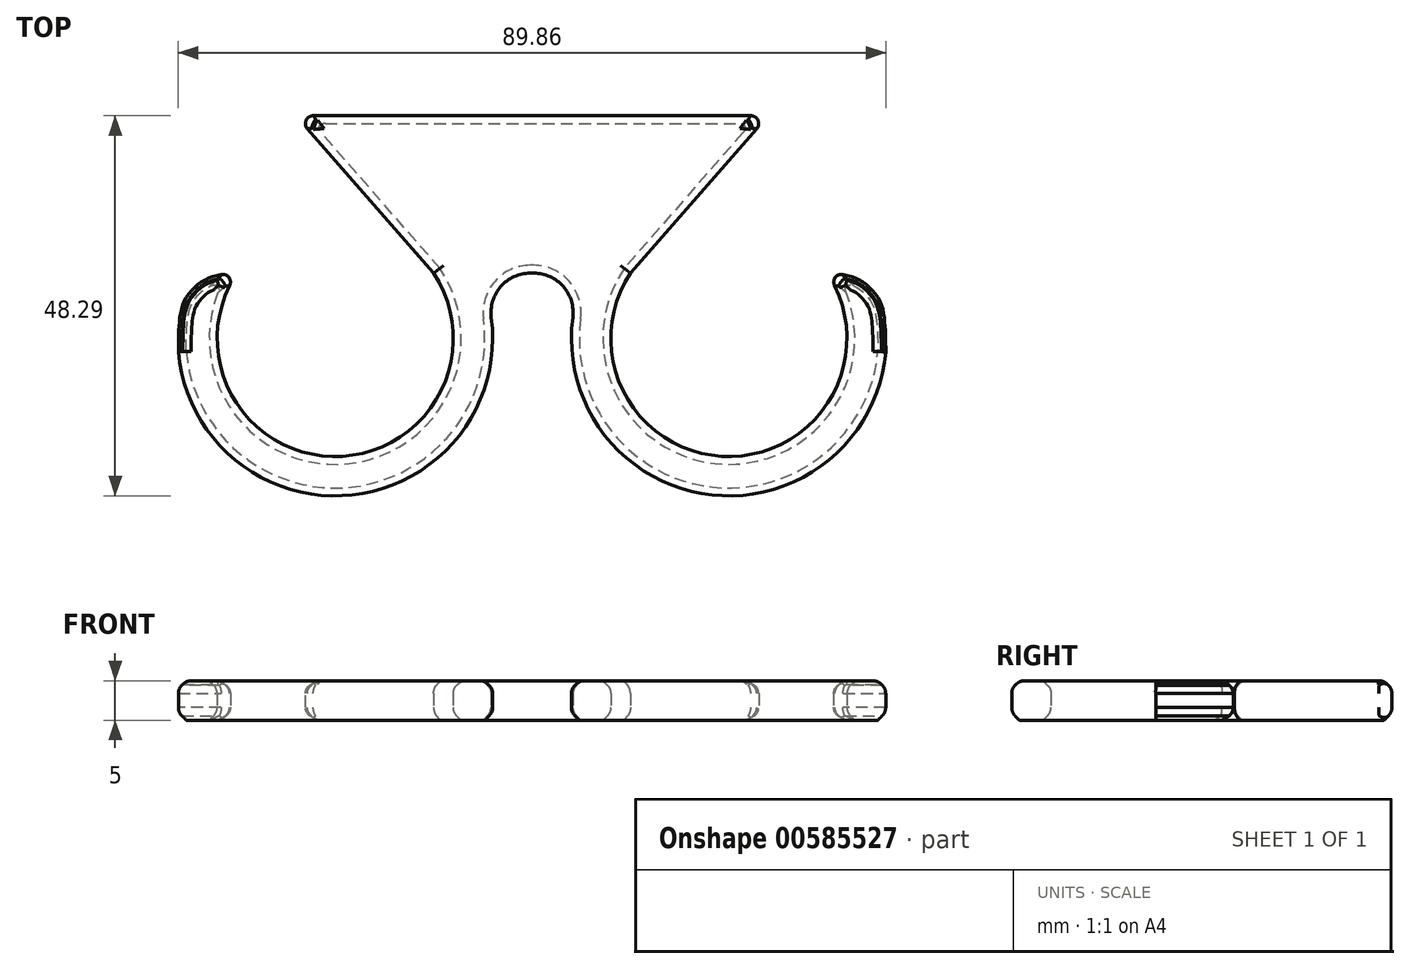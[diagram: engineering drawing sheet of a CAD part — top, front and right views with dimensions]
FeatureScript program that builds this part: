
annotation { "Feature Type Name" : "Feature", "Feature Type Description" : "" }
export const myFeature = defineFeature(function(context is Context, id is Id, definition is map)
    precondition{}
    {
        {
            var Q0;
            Q0=qCreatedBy(makeId("Top.planeOp"),FACE);
            var sketch = newSketch(context, id + "F0", { "sketchPlane" : qUnion([Q0])});
            skLineSegment(sketch, "E0", {"start": v(-30, 20) * mm, "end": v(0, 20) * mm});
            skLineSegment(sketch, "E1", {"start": v(-30, 20) * mm, "end": v(-12.5, 0) * mm});
            skLineSegment(sketch, "E2", {"start": v(-0.22, 0) * mm, "end": v(0, 0) * mm});
            skLineSegment(sketch, "E3", {"start": v(0, 0) * mm, "end": v(0, 20) * mm});
            skArc(sketch, "E4", {"start": v(-37.5, 0) * mm, "mid": v(-25, -23.3) * mm, "end": v(-12.5, 0) * mm});
            skArc(sketch, "E5.0", {"start": v(-44.93, -10) * mm, "mid": v(-22.83, -28.17) * mm, "end": v(-5.17, -5.66) * mm});
            skLineSegment(sketch, "E6", {"start": v(-44.93, -10) * mm, "end": v(-37.5, 0) * mm});
            skLineSegment(sketch, "E7.MirrorCS", {"start": v(30, 20) * mm, "end": v(0, 20) * mm});
            skLineSegment(sketch, "E8.MirrorCS", {"start": v(30, 20) * mm, "end": v(12.5, 0) * mm});
            skLineSegment(sketch, "E9.MirrorCS", {"start": v(0.22, 0) * mm, "end": v(0, 0) * mm});
            skArc(sketch, "E10.MirrorCS", {"start": v(44.93, -10) * mm, "mid": v(22.83, -28.17) * mm, "end": v(5.17, -5.66) * mm});
            skArc(sketch, "E11.MirrorCS", {"start": v(37.5, 0) * mm, "mid": v(25, -23.3) * mm, "end": v(12.5, 0) * mm});
            skLineSegment(sketch, "E12.MirrorCS", {"start": v(44.93, -10) * mm, "end": v(37.5, 0) * mm});
            skFitSpline(sketch, "E13", {"points": [v(-44.93, -10) * mm, v(-43.5, -2.5) * mm, v(-37.5, 0) * mm], "startDerivative": vector(0, 28.84) * mm, "endDerivative": vector(21.88, 0) * mm});
            skFitSpline(sketch, "E14.MirrorCS", {"points": [v(44.93, -10) * mm, v(43.5, -2.5) * mm, v(37.5, 0) * mm], "startDerivative": vector(0, 28.84) * mm, "endDerivative": vector(-21.88, 0) * mm});
            skArc(sketch, "E15.filletArc", {"start": v(-0.22, 0) * mm, "mid": v(-3.98, -1.7) * mm, "end": v(-5.17, -5.66) * mm});
            skArc(sketch, "E16.filletArc", {"start": v(5.17, -5.66) * mm, "mid": v(3.98, -1.7) * mm, "end": v(0.22, 0) * mm});
            skSolve(sketch);
        }
        {
            var Q0;
            Q0 = qSketchRegion(id + "F0", true);
            extrude(context, id + "F1", {"entities" : qUnion([Q0]), "depth" : 5 * mm, "offsetDistance" : 25 * mm});
        }
        {
            var Q0;
            Q0=makeQuery(id+"F1.opExtrude","CAP_FACE",FACE,{"disambiguationData":[OSD([sQuery(id+"F0.wireOp",EDGE,"E0"),sQuery(id+"F0.wireOp",EDGE,"E1"),sQuery(id+"F0.wireOp",EDGE,"E2"),sQuery(id+"F0.wireOp",EDGE,"E4"),sQuery(id+"F0.wireOp",EDGE,"E5.0"),sQuery(id+"F0.wireOp",EDGE,"E7.MirrorCS"),sQuery(id+"F0.wireOp",EDGE,"E8.MirrorCS"),sQuery(id+"F0.wireOp",EDGE,"E9.MirrorCS"),sQuery(id+"F0.wireOp",EDGE,"E10.MirrorCS"),sQuery(id+"F0.wireOp",EDGE,"E11.MirrorCS"),sQuery(id+"F0.wireOp",EDGE,"E13"),sQuery(id+"F0.wireOp",EDGE,"E14.MirrorCS"),sQuery(id+"F0.wireOp",EDGE,"E15.filletArc"),sQuery(id+"F0.wireOp",EDGE,"E16.filletArc")])],"isStart":false});
            var Q1;
            Q1=makeQuery(id+"F1.opExtrude","CAP_FACE",FACE,{"disambiguationData":[OSD([sQuery(id+"F0.wireOp",EDGE,"E0"),sQuery(id+"F0.wireOp",EDGE,"E1"),sQuery(id+"F0.wireOp",EDGE,"E2"),sQuery(id+"F0.wireOp",EDGE,"E4"),sQuery(id+"F0.wireOp",EDGE,"E5.0"),sQuery(id+"F0.wireOp",EDGE,"E7.MirrorCS"),sQuery(id+"F0.wireOp",EDGE,"E8.MirrorCS"),sQuery(id+"F0.wireOp",EDGE,"E9.MirrorCS"),sQuery(id+"F0.wireOp",EDGE,"E10.MirrorCS"),sQuery(id+"F0.wireOp",EDGE,"E11.MirrorCS"),sQuery(id+"F0.wireOp",EDGE,"E13"),sQuery(id+"F0.wireOp",EDGE,"E14.MirrorCS"),sQuery(id+"F0.wireOp",EDGE,"E15.filletArc"),sQuery(id+"F0.wireOp",EDGE,"E16.filletArc")])],"isStart":true});
            chamfer(context, id + "F2", {"entities" : qUnion([Q0, Q1]), "width" : 1 * mm, "tangentPropagation" : true});
        }
        {
            var Q0;
            {var subQ0=sQuery(id+"F0.wireOp",EDGE,"E5.0");Q0=makeQuery(id+"F2.opChamfer","BLEND_EDGE",EDGE,{"blendedFrom":[makeQuery(id+"F1.opExtrude","CAP_EDGE",EDGE,{"disambiguationData":[OSD([subQ0])],"isStart":true}),makeQuery(id+"F1.opExtrude","SWEPT_FACE",FACE,{"disambiguationData":[OSD([subQ0])]})],"blendedInto":[makeQuery(id+"F1.opExtrude","SWEPT_FACE",FACE,{"disambiguationData":[OSD([subQ0])]})]});}
            var Q1;
            {var subQ0=sQuery(id+"F0.wireOp",EDGE,"E15.filletArc");Q1=makeQuery(id+"F2.opChamfer","BLEND_EDGE",EDGE,{"blendedFrom":[makeQuery(id+"F1.opExtrude","CAP_EDGE",EDGE,{"disambiguationData":[OSD([subQ0])],"isStart":true}),makeQuery(id+"F1.opExtrude","SWEPT_FACE",FACE,{"disambiguationData":[OSD([subQ0])]})],"blendedInto":[makeQuery(id+"F1.opExtrude","SWEPT_FACE",FACE,{"disambiguationData":[OSD([subQ0])]})]});}
            var Q2;
            {var subQ0=sQuery(id+"F0.wireOp",EDGE,"E16.filletArc");Q2=makeQuery(id+"F2.opChamfer","BLEND_EDGE",EDGE,{"blendedFrom":[makeQuery(id+"F1.opExtrude","CAP_EDGE",EDGE,{"disambiguationData":[OSD([subQ0])],"isStart":true}),makeQuery(id+"F1.opExtrude","SWEPT_FACE",FACE,{"disambiguationData":[OSD([subQ0])]})],"blendedInto":[makeQuery(id+"F1.opExtrude","SWEPT_FACE",FACE,{"disambiguationData":[OSD([subQ0])]})]});}
            var Q3;
            {var subQ0=sQuery(id+"F0.wireOp",EDGE,"E9.MirrorCS");var subQ1=sQuery(id+"F0.wireOp",EDGE,"E2");Q3=makeQuery(id+"F2.opChamfer","BLEND_EDGE",EDGE,{"blendedFrom":[makeQuery(id+"F1.opExtrude","CAP_EDGE",EDGE,{"disambiguationData":[OSD([subQ1,subQ0])],"isStart":true}),makeQuery(id+"F1.opExtrude","SWEPT_FACE",FACE,{"disambiguationData":[OSD([subQ1,subQ0])]})],"blendedInto":[makeQuery(id+"F1.opExtrude","SWEPT_FACE",FACE,{"disambiguationData":[OSD([subQ1,subQ0])]})]});}
            var Q4;
            {var subQ0=sQuery(id+"F0.wireOp",EDGE,"E10.MirrorCS");Q4=makeQuery(id+"F2.opChamfer","BLEND_EDGE",EDGE,{"blendedFrom":[makeQuery(id+"F1.opExtrude","CAP_EDGE",EDGE,{"disambiguationData":[OSD([subQ0])],"isStart":true}),makeQuery(id+"F1.opExtrude","SWEPT_FACE",FACE,{"disambiguationData":[OSD([subQ0])]})],"blendedInto":[makeQuery(id+"F1.opExtrude","SWEPT_FACE",FACE,{"disambiguationData":[OSD([subQ0])]})]});}
            var Q5;
            {var subQ0=sQuery(id+"F0.wireOp",EDGE,"E13");Q5=makeQuery(id+"F2.opChamfer","BLEND_EDGE",EDGE,{"blendedFrom":[makeQuery(id+"F1.opExtrude","CAP_EDGE",EDGE,{"disambiguationData":[OSD([subQ0])],"isStart":true}),makeQuery(id+"F1.opExtrude","SWEPT_FACE",FACE,{"disambiguationData":[OSD([subQ0])]})],"blendedInto":[makeQuery(id+"F1.opExtrude","SWEPT_FACE",FACE,{"disambiguationData":[OSD([subQ0])]})]});}
            var Q6;
            {var subQ0=sQuery(id+"F0.wireOp",EDGE,"E4");Q6=makeQuery(id+"F2.opChamfer","BLEND_EDGE",EDGE,{"blendedFrom":[makeQuery(id+"F1.opExtrude","CAP_EDGE",EDGE,{"disambiguationData":[OSD([subQ0])],"isStart":true}),makeQuery(id+"F1.opExtrude","SWEPT_FACE",FACE,{"disambiguationData":[OSD([subQ0])]})],"blendedInto":[makeQuery(id+"F1.opExtrude","SWEPT_FACE",FACE,{"disambiguationData":[OSD([subQ0])]})]});}
            var Q7;
            {var subQ0=sQuery(id+"F0.wireOp",EDGE,"E1");Q7=makeQuery(id+"F2.opChamfer","BLEND_EDGE",EDGE,{"blendedFrom":[makeQuery(id+"F1.opExtrude","CAP_EDGE",EDGE,{"disambiguationData":[OSD([subQ0])],"isStart":true}),makeQuery(id+"F1.opExtrude","SWEPT_FACE",FACE,{"disambiguationData":[OSD([subQ0])]})],"blendedInto":[makeQuery(id+"F1.opExtrude","SWEPT_FACE",FACE,{"disambiguationData":[OSD([subQ0])]})]});}
            var Q8;
            {var subQ0=sQuery(id+"F0.wireOp",EDGE,"E7.MirrorCS");var subQ1=sQuery(id+"F0.wireOp",EDGE,"E0");Q8=makeQuery(id+"F2.opChamfer","BLEND_EDGE",EDGE,{"blendedFrom":[makeQuery(id+"F1.opExtrude","CAP_EDGE",EDGE,{"disambiguationData":[OSD([subQ1,subQ0])],"isStart":true}),makeQuery(id+"F1.opExtrude","SWEPT_FACE",FACE,{"disambiguationData":[OSD([subQ1,subQ0])]})],"blendedInto":[makeQuery(id+"F1.opExtrude","SWEPT_FACE",FACE,{"disambiguationData":[OSD([subQ1,subQ0])]})]});}
            var Q9;
            {var subQ0=sQuery(id+"F0.wireOp",EDGE,"E8.MirrorCS");Q9=makeQuery(id+"F2.opChamfer","BLEND_EDGE",EDGE,{"blendedFrom":[makeQuery(id+"F1.opExtrude","CAP_EDGE",EDGE,{"disambiguationData":[OSD([subQ0])],"isStart":true}),makeQuery(id+"F1.opExtrude","SWEPT_FACE",FACE,{"disambiguationData":[OSD([subQ0])]})],"blendedInto":[makeQuery(id+"F1.opExtrude","SWEPT_FACE",FACE,{"disambiguationData":[OSD([subQ0])]})]});}
            var Q10;
            {var subQ0=sQuery(id+"F0.wireOp",EDGE,"E11.MirrorCS");Q10=makeQuery(id+"F2.opChamfer","BLEND_EDGE",EDGE,{"blendedFrom":[makeQuery(id+"F1.opExtrude","CAP_EDGE",EDGE,{"disambiguationData":[OSD([subQ0])],"isStart":true}),makeQuery(id+"F1.opExtrude","SWEPT_FACE",FACE,{"disambiguationData":[OSD([subQ0])]})],"blendedInto":[makeQuery(id+"F1.opExtrude","SWEPT_FACE",FACE,{"disambiguationData":[OSD([subQ0])]})]});}
            var Q11;
            {var subQ0=sQuery(id+"F0.wireOp",EDGE,"E14.MirrorCS");Q11=makeQuery(id+"F2.opChamfer","BLEND_EDGE",EDGE,{"blendedFrom":[makeQuery(id+"F1.opExtrude","CAP_EDGE",EDGE,{"disambiguationData":[OSD([subQ0])],"isStart":true}),makeQuery(id+"F1.opExtrude","SWEPT_FACE",FACE,{"disambiguationData":[OSD([subQ0])]})],"blendedInto":[makeQuery(id+"F1.opExtrude","SWEPT_FACE",FACE,{"disambiguationData":[OSD([subQ0])]})]});}
            var Q12;
            Q12=makeQuery(id+"F1.opExtrude","CAP_FACE",FACE,{"disambiguationData":[OSD([sQuery(id+"F0.wireOp",EDGE,"E0"),sQuery(id+"F0.wireOp",EDGE,"E1"),sQuery(id+"F0.wireOp",EDGE,"E2"),sQuery(id+"F0.wireOp",EDGE,"E4"),sQuery(id+"F0.wireOp",EDGE,"E5.0"),sQuery(id+"F0.wireOp",EDGE,"E7.MirrorCS"),sQuery(id+"F0.wireOp",EDGE,"E8.MirrorCS"),sQuery(id+"F0.wireOp",EDGE,"E9.MirrorCS"),sQuery(id+"F0.wireOp",EDGE,"E10.MirrorCS"),sQuery(id+"F0.wireOp",EDGE,"E11.MirrorCS"),sQuery(id+"F0.wireOp",EDGE,"E13"),sQuery(id+"F0.wireOp",EDGE,"E14.MirrorCS"),sQuery(id+"F0.wireOp",EDGE,"E15.filletArc"),sQuery(id+"F0.wireOp",EDGE,"E16.filletArc")])],"isStart":false});
            var Q13;
            {var subQ0=sQuery(id+"F0.wireOp",EDGE,"E14.MirrorCS");Q13=makeQuery(id+"F2.opChamfer","BLEND_EDGE",EDGE,{"blendedFrom":[makeQuery(id+"F1.opExtrude","CAP_EDGE",EDGE,{"disambiguationData":[OSD([subQ0])],"isStart":false}),makeQuery(id+"F1.opExtrude","SWEPT_FACE",FACE,{"disambiguationData":[OSD([subQ0])]})],"blendedInto":[makeQuery(id+"F1.opExtrude","SWEPT_FACE",FACE,{"disambiguationData":[OSD([subQ0])]})]});}
            var Q14;
            {var subQ0=sQuery(id+"F0.wireOp",EDGE,"E10.MirrorCS");Q14=makeQuery(id+"F2.opChamfer","BLEND_EDGE",EDGE,{"blendedFrom":[makeQuery(id+"F1.opExtrude","CAP_EDGE",EDGE,{"disambiguationData":[OSD([subQ0])],"isStart":false}),makeQuery(id+"F1.opExtrude","SWEPT_FACE",FACE,{"disambiguationData":[OSD([subQ0])]})],"blendedInto":[makeQuery(id+"F1.opExtrude","SWEPT_FACE",FACE,{"disambiguationData":[OSD([subQ0])]})]});}
            var Q15;
            {var subQ0=sQuery(id+"F0.wireOp",EDGE,"E11.MirrorCS");Q15=makeQuery(id+"F2.opChamfer","BLEND_EDGE",EDGE,{"blendedFrom":[makeQuery(id+"F1.opExtrude","CAP_EDGE",EDGE,{"disambiguationData":[OSD([subQ0])],"isStart":false}),makeQuery(id+"F1.opExtrude","SWEPT_FACE",FACE,{"disambiguationData":[OSD([subQ0])]})],"blendedInto":[makeQuery(id+"F1.opExtrude","SWEPT_FACE",FACE,{"disambiguationData":[OSD([subQ0])]})]});}
            var Q16;
            {var subQ0=sQuery(id+"F0.wireOp",EDGE,"E8.MirrorCS");Q16=makeQuery(id+"F2.opChamfer","BLEND_EDGE",EDGE,{"blendedFrom":[makeQuery(id+"F1.opExtrude","CAP_EDGE",EDGE,{"disambiguationData":[OSD([subQ0])],"isStart":false}),makeQuery(id+"F1.opExtrude","SWEPT_FACE",FACE,{"disambiguationData":[OSD([subQ0])]})],"blendedInto":[makeQuery(id+"F1.opExtrude","SWEPT_FACE",FACE,{"disambiguationData":[OSD([subQ0])]})]});}
            var Q17;
            {var subQ0=sQuery(id+"F0.wireOp",EDGE,"E7.MirrorCS");var subQ1=sQuery(id+"F0.wireOp",EDGE,"E0");Q17=makeQuery(id+"F2.opChamfer","BLEND_EDGE",EDGE,{"blendedFrom":[makeQuery(id+"F1.opExtrude","CAP_EDGE",EDGE,{"disambiguationData":[OSD([subQ1,subQ0])],"isStart":false}),makeQuery(id+"F1.opExtrude","SWEPT_FACE",FACE,{"disambiguationData":[OSD([subQ1,subQ0])]})],"blendedInto":[makeQuery(id+"F1.opExtrude","SWEPT_FACE",FACE,{"disambiguationData":[OSD([subQ1,subQ0])]})]});}
            var Q18;
            {var subQ0=sQuery(id+"F0.wireOp",EDGE,"E1");Q18=makeQuery(id+"F2.opChamfer","BLEND_EDGE",EDGE,{"blendedFrom":[makeQuery(id+"F1.opExtrude","CAP_EDGE",EDGE,{"disambiguationData":[OSD([subQ0])],"isStart":false}),makeQuery(id+"F1.opExtrude","SWEPT_FACE",FACE,{"disambiguationData":[OSD([subQ0])]})],"blendedInto":[makeQuery(id+"F1.opExtrude","SWEPT_FACE",FACE,{"disambiguationData":[OSD([subQ0])]})]});}
            var Q19;
            {var subQ0=sQuery(id+"F0.wireOp",EDGE,"E4");Q19=makeQuery(id+"F2.opChamfer","BLEND_EDGE",EDGE,{"blendedFrom":[makeQuery(id+"F1.opExtrude","CAP_EDGE",EDGE,{"disambiguationData":[OSD([subQ0])],"isStart":false}),makeQuery(id+"F1.opExtrude","SWEPT_FACE",FACE,{"disambiguationData":[OSD([subQ0])]})],"blendedInto":[makeQuery(id+"F1.opExtrude","SWEPT_FACE",FACE,{"disambiguationData":[OSD([subQ0])]})]});}
            var Q20;
            {var subQ0=sQuery(id+"F0.wireOp",EDGE,"E5.0");Q20=makeQuery(id+"F2.opChamfer","BLEND_EDGE",EDGE,{"blendedFrom":[makeQuery(id+"F1.opExtrude","CAP_EDGE",EDGE,{"disambiguationData":[OSD([subQ0])],"isStart":false}),makeQuery(id+"F1.opExtrude","SWEPT_FACE",FACE,{"disambiguationData":[OSD([subQ0])]})],"blendedInto":[makeQuery(id+"F1.opExtrude","SWEPT_FACE",FACE,{"disambiguationData":[OSD([subQ0])]})]});}
            var Q21;
            {var subQ0=sQuery(id+"F0.wireOp",EDGE,"E13");Q21=makeQuery(id+"F2.opChamfer","BLEND_EDGE",EDGE,{"blendedFrom":[makeQuery(id+"F1.opExtrude","CAP_EDGE",EDGE,{"disambiguationData":[OSD([subQ0])],"isStart":false}),makeQuery(id+"F1.opExtrude","SWEPT_FACE",FACE,{"disambiguationData":[OSD([subQ0])]})],"blendedInto":[makeQuery(id+"F1.opExtrude","SWEPT_FACE",FACE,{"disambiguationData":[OSD([subQ0])]})]});}
            var Q22;
            {var subQ0=sQuery(id+"F0.wireOp",EDGE,"E16.filletArc");Q22=makeQuery(id+"F2.opChamfer","BLEND_EDGE",EDGE,{"blendedFrom":[makeQuery(id+"F1.opExtrude","CAP_EDGE",EDGE,{"disambiguationData":[OSD([subQ0])],"isStart":false}),makeQuery(id+"F1.opExtrude","SWEPT_FACE",FACE,{"disambiguationData":[OSD([subQ0])]})],"blendedInto":[makeQuery(id+"F1.opExtrude","SWEPT_FACE",FACE,{"disambiguationData":[OSD([subQ0])]})]});}
            var Q23;
            {var subQ0=sQuery(id+"F0.wireOp",EDGE,"E15.filletArc");Q23=makeQuery(id+"F2.opChamfer","BLEND_EDGE",EDGE,{"blendedFrom":[makeQuery(id+"F1.opExtrude","CAP_EDGE",EDGE,{"disambiguationData":[OSD([subQ0])],"isStart":false}),makeQuery(id+"F1.opExtrude","SWEPT_FACE",FACE,{"disambiguationData":[OSD([subQ0])]})],"blendedInto":[makeQuery(id+"F1.opExtrude","SWEPT_FACE",FACE,{"disambiguationData":[OSD([subQ0])]})]});}
            var Q24;
            {var subQ0=sQuery(id+"F0.wireOp",EDGE,"E9.MirrorCS");var subQ1=sQuery(id+"F0.wireOp",EDGE,"E2");Q24=makeQuery(id+"F2.opChamfer","BLEND_EDGE",EDGE,{"blendedFrom":[makeQuery(id+"F1.opExtrude","CAP_EDGE",EDGE,{"disambiguationData":[OSD([subQ1,subQ0])],"isStart":false}),makeQuery(id+"F1.opExtrude","SWEPT_FACE",FACE,{"disambiguationData":[OSD([subQ1,subQ0])]})],"blendedInto":[makeQuery(id+"F1.opExtrude","SWEPT_FACE",FACE,{"disambiguationData":[OSD([subQ1,subQ0])]})]});}
            fillet(context, id + "F3", {"entities" : qUnion([Q0, Q1, Q2, Q3, Q4, Q5, Q6, Q7, Q8, Q9, Q10, Q11, Q12, Q13, Q14, Q15, Q16, Q17, Q18, Q19, Q20, Q21, Q22, Q23, Q24]), "radius" : 1.5 * mm, "tangentPropagation" : true, "allowEdgeOverflow" : false});
        }
        {
            var Q0;
            Q0=makeQuery(id+"F1.opExtrude","SWEPT_EDGE",EDGE,{"disambiguationData":[OSD([sQuery(id+"F0.wireOp",EDGE,"E0"),sQuery(id+"F0.wireOp",EDGE,"E1")])]});
            var Q1;
            Q1=makeQuery(id+"F1.opExtrude","SWEPT_EDGE",EDGE,{"disambiguationData":[OSD([sQuery(id+"F0.wireOp",EDGE,"E7.MirrorCS"),sQuery(id+"F0.wireOp",EDGE,"E8.MirrorCS")])]});
            var Q2;
            Q2=makeQuery(id+"F1.opExtrude","SWEPT_EDGE",EDGE,{"disambiguationData":[OSD([sQuery(id+"F0.wireOp",EDGE,"E11.MirrorCS"),sQuery(id+"F0.wireOp",EDGE,"E12.MirrorCS"),sQuery(id+"F0.wireOp",EDGE,"E14.MirrorCS")])]});
            var Q3;
            Q3=makeQuery(id+"F1.opExtrude","SWEPT_EDGE",EDGE,{"disambiguationData":[OSD([sQuery(id+"F0.wireOp",EDGE,"E4"),sQuery(id+"F0.wireOp",EDGE,"E6"),sQuery(id+"F0.wireOp",EDGE,"E13")])]});
            fillet(context, id + "F4", {"entities" : qUnion([Q0, Q1, Q2, Q3]), "radius" : 1 * mm, "tangentPropagation" : true, "allowEdgeOverflow" : false});
        }
    });
